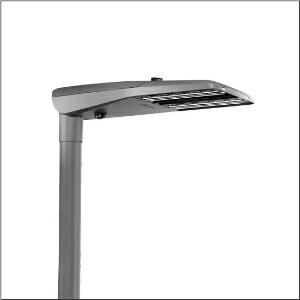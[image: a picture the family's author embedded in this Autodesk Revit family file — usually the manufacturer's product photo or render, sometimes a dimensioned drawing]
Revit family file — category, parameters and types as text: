
# Revit family: streetlight_sl_11_iq_midi___pc-r_5xc3f21y08me_3682
name_source: partatom
category: Lighting Fixtures
units: mm (PartAtom-declared; Revit-internal decimal feet)

## family parameters
Cut with Voids When Loaded = No
Host = Face
Light Source = No
Part Type = Normal
Room Calculation Point = No
Round Connector Dimension = Use Diameter
Shared = No

## types (1)
- --- (1 x LED, 12730 lm, 122.8 W, 2200K)
    Apparent Load = 123 VA
    CIE Flux Codes = 37 73 96 100 100
    Color Rendering = 70
    Color Temperature = 2200K
    Default Elevation = 1800 mm
    Description = Streetlight SL 11 iQ midi, mast luminaire, primary light control with 3 zone facetted reflector, of plastic, silver coated, highly specular, primary optical cover: cover, of PMMA, transparent, light distribution: PC-R, light emission: direct distribution, primary light characteristic: asymmetric, right, installation type: post-top, side-entry, LED, High Power LED, rated luminous flux: 12.730lm, luminous efficacy: 104lm/W, light colour: 722, colour temperature: 2200K, control: presetting dimming logarithmic, Street-Remote, Auto-Match, Temp-Guard, Lumen-Switch, Night-Set, Smart-Wire, Light-Fading, Desk-Remote (wireless, voltage-free reading and setting of iQ features in the workshop via application-optimized NFC function/RFID function), optimised constant luminous flux control (CLO 2.0), with cable H07RN-F 5x 1.5mm², mains connection: 230..240V, AC, 50/60Hz, connection cable pre-assembled, cable length: 12,5m, start of lifetime: 123W, end of service life: 130W, reduction: 56W, luminaire housing, of diecast aluminium, powder-coated, Siteco® metallic grey (DB 702S), please order mast flange separately, inclination adjustable without tools: 0°, 5°, 10°, 15° (post-top) | 0°, -5°, -10°, -15° (side-entry), sealing non-destructively replaceable, multi-level sealing system, length: 780mm, width: 376mm, height: 118mm, mast flange for spigot size: 42mm (side-entry): 5XC10008XM4, 60/48mm (side-entry/post-top): 5XC10108XM2, 76/60mm (side-entry/post-top): 5XC10108XM1, equipment: Power, Smart Interface below and above, protection rating (complete): IP66, insulation class (complete): insulation class II (safety insulation), certification: CE, ENEC, VDE, UKCA, impact resistance: IK09, permissible operating ambient temperature for outdoor applications: -25..+50°C, standard-compliant lighting for roads and squares, Environmental Product Declaration (EPD) tested and certified by an independent institute, packaging unit: 1 piece

Light Distribution: PC-R
    Height = 118 mm
    Lamp = 1 x LED
    Lamp Light Flux = 12730 lm
    Lamp Power = 122.8 W
    Lamp count = 1
    Length = 780 mm
    Luminous efficacy = 104 lm/W
    Manufacturer = Siteco
    ModVariant = No
    Model = 5XC3F21Y08ME
    Number of Poles = 1
    OnlyDefault = Yes
    Power Factor = 1
    Product Name = Streetlight SL 11 iQ midi | PC-R
    Product group = mast luminaire | pylon top
    ProductGroupID = 6100
    Protection Class = Protection class II
    Protection Degree = IP 66
    RLX_Detail_Level = 1
    RLX_Emergency_Light_Flux = 0 lm
    RLX_Emergency_Type = 0
    RLX_Emergency_Type_DB = No
    RlxData = <blob elided: 73541 chars, md5=f6842df3>
    Socket = socket
    Standby Power = 0 W
    System Light Flux = 12729 lm
    System Power = 123 W
    Type Comments = factory setting: luminous flux: 100 % | dim-lin: 254 | 553 mA
    Type Image = l_1004429.jpg
    URL = http://relux.com
    VarID = @adj_058147
    Voltage = 0 V
    Weight = 0.00 kg
    Width = 376 mm

## geometry (parser evidence)
native form markers: Blend x4, Sweep x12
no freeform markers — native parametric forms only
